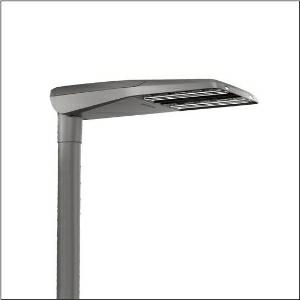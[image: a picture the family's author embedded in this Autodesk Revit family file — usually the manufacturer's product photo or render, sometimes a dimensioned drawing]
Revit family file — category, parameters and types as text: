
# Revit family: streetlight_sl_11_iq_midi___st1_0ab_5xc3n51f08me_d360
name_source: partatom
category: Lighting Fixtures
units: mm (PartAtom-declared; Revit-internal decimal feet)

## family parameters
Cut with Voids When Loaded = No
Host = Face
Light Source = No
Part Type = Normal
Room Calculation Point = No
Round Connector Dimension = Use Diameter
Shared = No

## types (1)
- --- (1 x LED, 15260 lm, 124.7 W, 3000K)
    Apparent Load = 125 VA
    CIE Flux Codes = 29 63 95 100 100
    Color Rendering = 70
    Color Temperature = 3000K
    Default Elevation = 1800 mm
    Description = Streetlight SL 11 iQ midi, mast luminaire, primary light control with 3 zone facetted reflector, of plastic, silver coated, highly specular, primary optical cover: cover, of PMMA, transparent, light distribution: ST1.0aB, light emission: direct distribution, primary light characteristic: asymmetric, installation type: post-top, side-entry, lamps: LED, High Power LED, rated values: 15.260lm | 124,7W | 122,4lm/W (begin service life); end service life: 15.260lm | 132,2W; at 50% lumin. flux: 7.630lm | 57,2W | 133,4lm/W, colour temperature: 3000K, colour rendering: CRI > 70, light colour: 730, light setting 1 begin service life: 100% | 15.260lm | 124,7W | 122,4lm/W | 3.000K, light setting 1 end service life: 132,2W, further light settings possible, control: optimised constant luminous flux control (CLO 2.0), Street-Remote, Desk-Remote (wireless, voltage-free reading and setting of iQ features in the workshop via application-optimized NFC function/RFID function), Light-Fading, Smart-Wire, Night-Set, Lumen-Switch, Temp-Guard, Auto-Match, with cable H07RN-F 3x 1.5mm², mains connection: 230..240V, AC, 50/60Hz, connection cable pre-assembled, cable length: 12,5m, luminaire housing, of diecast aluminium, powder-coated, SITECO metallic grey (DB 702S), please order mast flange separately, inclination adjustable without tools: 0°, 5°, 10°, 15° (post-top) | 0°, -5°, -10°, -15° (side-entry), sealing non-destructively replaceable, multi-level sealing system, length: 780mm, width: 376mm, height: 118mm, mast flange for spigot size: 42mm (side-entry): 5XC10008XM4, 60/48mm (side-entry/post-top): 5XC10108XM2, 76/60mm (side-entry/post-top): 5XC10108XM1, equipment: Power, protection rating (complete): IP66, insulation class (complete): insulation class II (safety insulation), certification: CE, ENEC, ENEC+, VDE, impact resistance: IK10, permissible operating ambient temperature for outdoor applications: -25..+50°C, standard-compliant lighting for roads and squares, Environmental Product Declaration (EPD) tested and certified by an independent institute, packaging unit: 1 piece

Light Distribution: ST1.0aB
    Height = 118 mm
    Lamp = 1 x LED
    Lamp Light Flux = 15260 lm
    Lamp Power = 124.7 W
    Lamp count = 1
    Length = 780 mm
    Luminous efficacy = 122 lm/W
    Manufacturer = Siteco
    ModVariant = No
    Model = 5XC3N51F08ME
    Number of Poles = 1
    OnlyDefault = Yes
    Power Factor = 1
    Product Name = Streetlight SL 11 iQ midi | ST1.0aB
    Product group = mast luminaire | pylon top
    ProductGroupID = 6100
    Protection Class = Protection class II
    Protection Degree = IP 66
    RLX_Detail_Level = 1
    RLX_Emergency_Light_Flux = 0 lm
    RLX_Emergency_Type = 0
    RLX_Emergency_Type_DB = No
    RlxData = <blob elided: 70329 chars, md5=d88dfa7a>
    Socket = socket
    Standby Power = 0 W
    System Light Flux = 15260 lm
    System Power = 125 W
    Type Comments = factory setting: luminous flux: 100 % | dim-lin: 254 | 557 mA
    Type Image = l_1005960.jpg
    URL = http://relux.com
    VarID = @adj_091781
    Voltage = 0 V
    Weight = 0.00 kg
    Width = 376 mm

## geometry (parser evidence)
native form markers: Blend x4, Sweep x12
no freeform markers — native parametric forms only
